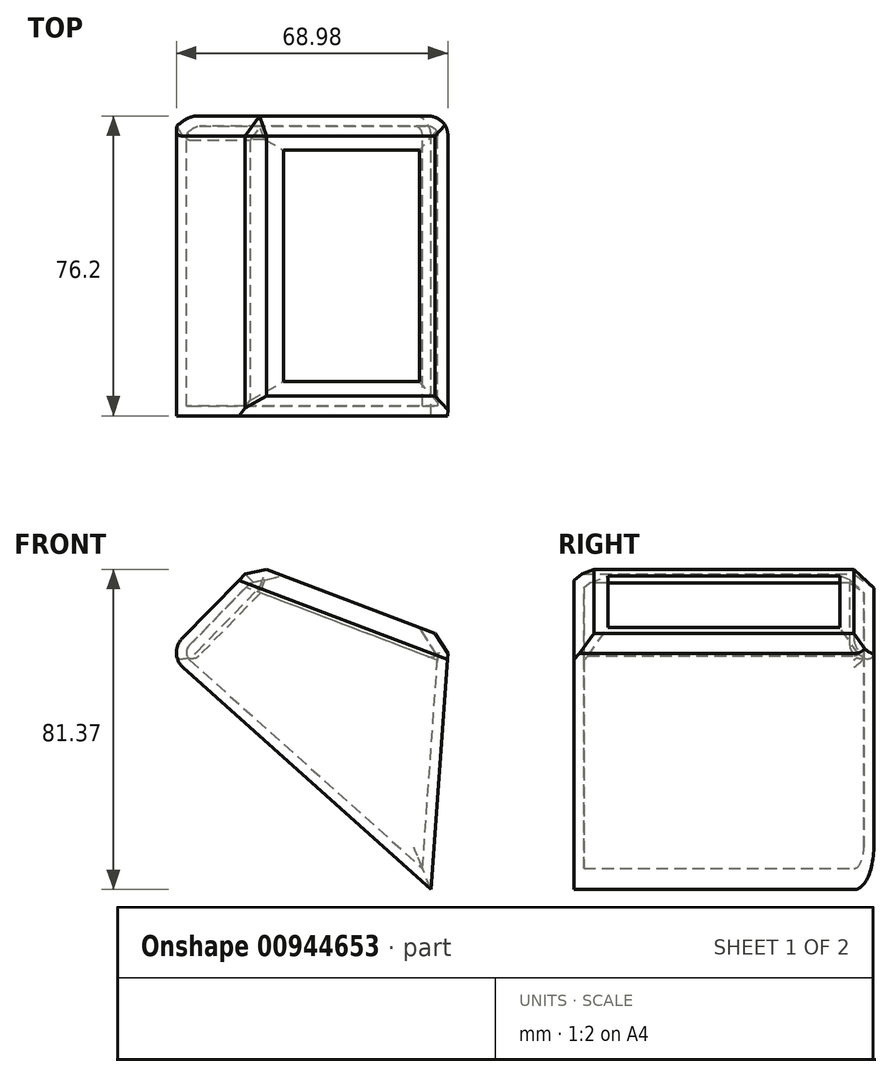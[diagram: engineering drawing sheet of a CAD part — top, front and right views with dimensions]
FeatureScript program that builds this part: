
annotation { "Feature Type Name" : "Feature", "Feature Type Description" : "" }
export const myFeature = defineFeature(function(context is Context, id is Id, definition is map)
    precondition{}
    {
        {
            var Q0;
            Q0=qCreatedBy(makeId("Front.planeOp"),FACE);
            var sketch = newSketch(context, id + "F0", { "sketchPlane" : qUnion([Q0])});
            skLineSegment(sketch, "E0", {"start": v(-42.86, 19.25) * mm, "end": v(24.1, -40.73) * mm});
            skLineSegment(sketch, "E1", {"start": v(24.1, -40.73) * mm, "end": v(28.63, 23) * mm});
            skLineSegment(sketch, "E2", {"start": v(28.63, 23) * mm, "end": v(-20.86, 41.83) * mm});
            skLineSegment(sketch, "E3", {"start": v(-20.86, 41.83) * mm, "end": v(-42.86, 19.25) * mm});
            skSolve(sketch);
        }
        {
            var Q0;
            Q0=makeQuery(id+"F0.imprint","IMPRINT",FACE,{"disambiguationData":[TD([[makeQuery(id+"F0.imprint","IMPRINT",EDGE,{"derivedFrom":sQuery(id+"F0.wireOp",EDGE,"E0")}),1.0]])]});
            extrude(context, id + "F1", {"entities" : qUnion([Q0]), "depth" : 76.2 * mm, "offsetDistance" : 25.4 * mm});
        }
        {
            var Q0;
            Q0=makeQuery(id+"F1.opExtrude","CAP_EDGE",EDGE,{"disambiguationData":[OSD([sQuery(id+"F0.wireOp",EDGE,"E2")])],"isStart":false});
            var Q1;
            Q1=makeQuery(id+"F1.opExtrude","SWEPT_EDGE",EDGE,{"disambiguationData":[OSD([sQuery(id+"F0.wireOp",EDGE,"E1"),sQuery(id+"F0.wireOp",EDGE,"E2")])]});
            var Q2;
            Q2=makeQuery(id+"F1.opExtrude","CAP_EDGE",EDGE,{"disambiguationData":[OSD([sQuery(id+"F0.wireOp",EDGE,"E2")])],"isStart":true});
            var Q3;
            Q3=makeQuery(id+"F1.opExtrude","SWEPT_EDGE",EDGE,{"disambiguationData":[OSD([sQuery(id+"F0.wireOp",EDGE,"E2"),sQuery(id+"F0.wireOp",EDGE,"E3")])]});
            var Q4;
            Q4=makeQuery(id+"F1.opExtrude","CAP_EDGE",EDGE,{"disambiguationData":[OSD([sQuery(id+"F0.wireOp",EDGE,"E3")])],"isStart":true});
            chamfer(context, id + "F2", {"entities" : qUnion([Q0, Q1, Q2, Q3, Q4]), "width" : 5.08 * mm, "tangentPropagation" : true});
        }
        {
            var Q0;
            Q0=makeQuery(id+"F1.opExtrude","CAP_EDGE",EDGE,{"disambiguationData":[OSD([sQuery(id+"F0.wireOp",EDGE,"E0")])],"isStart":true});
            var Q1;
            Q1=makeQuery(id+"F1.opExtrude","CAP_EDGE",EDGE,{"disambiguationData":[OSD([sQuery(id+"F0.wireOp",EDGE,"E1")])],"isStart":true});
            var Q2;
            Q2=makeQuery(id+"F1.opExtrude","SWEPT_EDGE",EDGE,{"disambiguationData":[OSD([sQuery(id+"F0.wireOp",EDGE,"E0"),sQuery(id+"F0.wireOp",EDGE,"E3")])]});
            fillet(context, id + "F3", {"entities" : qUnion([Q0, Q1, Q2]), "radius" : 5.08 * mm, "tangentPropagation" : true, "allowEdgeOverflow" : false});
        }
        {
            var Q0;
            Q0=makeQuery(id+"F1.opExtrude","SWEPT_FACE",FACE,{"disambiguationData":[OSD([sQuery(id+"F0.wireOp",EDGE,"E2")])]});
            shell(context, id + "F4", {"entities" : qUnion([Q0]), "thickness" : 2.54 * mm});
        }
    });
